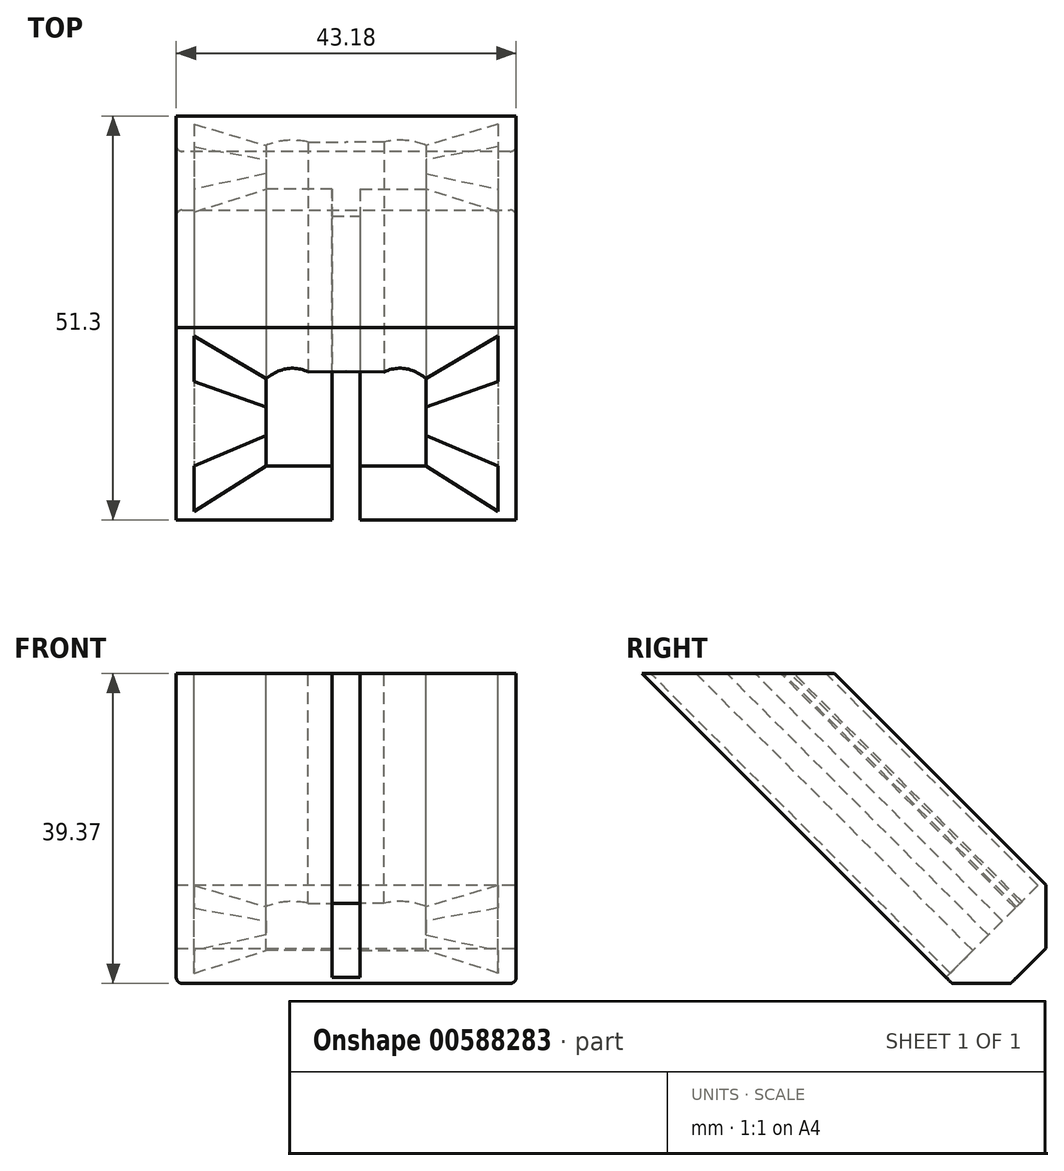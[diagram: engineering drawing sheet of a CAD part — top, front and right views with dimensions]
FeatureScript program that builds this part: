
annotation { "Feature Type Name" : "Feature", "Feature Type Description" : "" }
export const myFeature = defineFeature(function(context is Context, id is Id, definition is map)
    precondition{}
    {
        {
            var Q0;
            Q0=qCreatedBy(makeId("Front.planeOp"),FACE);
            var sketch = newSketch(context, id + "F0", { "sketchPlane" : qUnion([Q0])});
            skLineSegment(sketch, "E0.bottom", {"start": v(21.59, -8.64) * mm, "end": v(-21.6, -8.64) * mm});
            skLineSegment(sketch, "E0.top", {"start": v(21.59, 8.64) * mm, "end": v(-21.59, 8.64) * mm});
            skLineSegment(sketch, "E0.left", {"start": v(21.59, -8.64) * mm, "end": v(21.59, 8.64) * mm});
            skLineSegment(sketch, "E0.right", {"start": v(-21.6, -8.64) * mm, "end": v(-21.59, 8.64) * mm});
            skPoint(sketch, "E0.middle", {"position": v(0, 0) * mm});
            skSolve(sketch);
        }
        {
            var Q0;
            Q0=qCreatedBy(makeId("Front.planeOp"),FACE);
            var sketch = newSketch(context, id + "F1", { "sketchPlane" : qUnion([Q0])});
            skPoint(sketch, "E1.middle", {"position": v(0, 0) * mm});
            skLineSegment(sketch, "E2.left", {"start": v(10.16, 1.5) * mm, "end": v(10.16, -1.03) * mm});
            skLineSegment(sketch, "E3", {"start": v(19.3, 3.81) * mm, "end": v(10.16, 1.5) * mm});
            skLineSegment(sketch, "E4", {"start": v(10.16, -1.03) * mm, "end": v(19.3, -3.81) * mm});
            skLineSegment(sketch, "E5.left", {"start": v(19.3, 7.87) * mm, "end": v(19.3, 3.81) * mm});
            skLineSegment(sketch, "E6", {"start": v(19.3, -7.87) * mm, "end": v(10.16, -3.81) * mm});
            skLineSegment(sketch, "E7", {"start": v(19.3, 7.87) * mm, "end": v(10.16, 4.05) * mm});
            skLineSegment(sketch, "E8", {"start": v(1.78, -7.87) * mm, "end": v(1.78, -3.81) * mm});
            skLineSegment(sketch, "E9.trimOffspring", {"start": v(1.78, -3.81) * mm, "end": v(10.16, -3.81) * mm});
            skLineSegment(sketch, "E10.trimOffspring", {"start": v(19.3, -3.8) * mm, "end": v(19.3, -7.87) * mm});
            skLineSegment(sketch, "E11", {"start": v(1.78, -7.87) * mm, "end": v(1.78, -8.98) * mm});
            skArc(sketch, "E12", {"start": v(10.16, 4.05) * mm, "mid": v(7.57, 4.95) * mm, "end": v(4.83, 4.67) * mm});
            skLineSegment(sketch, "E13", {"start": v(4.83, 4.67) * mm, "end": v(0, 4.69) * mm});
            skLineSegment(sketch, "E14.MirrorCS", {"start": v(-10.16, 1.5) * mm, "end": v(-10.16, -1.03) * mm});
            skLineSegment(sketch, "E15.MirrorCS", {"start": v(-10.16, -1.03) * mm, "end": v(-19.3, -3.81) * mm});
            skLineSegment(sketch, "E16.MirrorCS", {"start": v(-19.3, -3.8) * mm, "end": v(-19.3, -7.87) * mm});
            skLineSegment(sketch, "E17.MirrorCS", {"start": v(-1.78, -7.87) * mm, "end": v(-1.78, -3.81) * mm});
            skLineSegment(sketch, "E18.MirrorCS", {"start": v(-4.83, 4.67) * mm, "end": v(0, 4.69) * mm});
            skLineSegment(sketch, "E19.MirrorCS", {"start": v(-1.78, -7.87) * mm, "end": v(-1.78, -8.98) * mm});
            skLineSegment(sketch, "E20.MirrorCS", {"start": v(-19.3, -7.87) * mm, "end": v(-10.16, -3.81) * mm});
            skLineSegment(sketch, "E21.MirrorCS", {"start": v(-19.3, 3.81) * mm, "end": v(-10.16, 1.5) * mm});
            skLineSegment(sketch, "E22.MirrorCS", {"start": v(-19.3, 7.87) * mm, "end": v(-10.16, 4.05) * mm});
            skArc(sketch, "E23.MirrorCS", {"start": v(-10.16, 4.05) * mm, "mid": v(-7.57, 4.95) * mm, "end": v(-4.83, 4.67) * mm});
            skLineSegment(sketch, "E24.MirrorCS", {"start": v(-19.3, 7.87) * mm, "end": v(-19.3, 3.81) * mm});
            skLineSegment(sketch, "E25.MirrorCS", {"start": v(-1.78, -3.81) * mm, "end": v(-10.16, -3.81) * mm});
            skLineSegment(sketch, "E26", {"start": v(-1.78, -8.98) * mm, "end": v(1.78, -8.98) * mm});
            skSolve(sketch);
        }
        {
            var Q0;
            Q0=makeQuery(id+"F0.imprint","IMPRINT",FACE,{"disambiguationData":[TD([[makeQuery(id+"F0.imprint","IMPRINT",EDGE,{"derivedFrom":sQuery(id+"F0.wireOp",EDGE,"E0.bottom")}),-1.0]])]});
            extrude(context, id + "F2", {"entities" : qUnion([Q0]), "oppositeDirection" : true, "depth" : 76.2 * mm, "offsetDistance" : 25.4 * mm});
        }
        {
            var Q0;
            Q0 = qSketchRegion(id + "F1", true);
            extrude(context, id + "F3", {"entities" : qUnion([Q0]), "operationType" : NewBodyOperationType.REMOVE, "oppositeDirection" : true, "depth" : 69.85 * mm, "offsetDistance" : 25.4 * mm});
        }
        {
            var Q0;
            Q0=makeQuery(id+"F2.opExtrude","SWEPT_BODY",BODY,{"disambiguationData":[OSD([sQuery(id+"F0.wireOp",EDGE,"E0.bottom"),sQuery(id+"F0.wireOp",EDGE,"E0.top"),sQuery(id+"F0.wireOp",EDGE,"E0.left"),sQuery(id+"F0.wireOp",EDGE,"E0.right")])]});
            var Q1;
            Q1=qCreatedBy(makeId("Front.planeOp"),FACE);
            transform(context, id + "F4", {"entities" : qUnion([Q0]), "transformType" : TransformType.TRANSLATION_DISTANCE, "transformDirection" : qUnion([Q1]), "distance" : 38.1 * mm, "makeCopy" : false});
        }
        {
            var Q0;
            Q0=qCreatedBy(makeId("Top.planeOp"),FACE);
            var sketch = newSketch(context, id + "F5", { "sketchPlane" : qUnion([Q0])});
            skLineSegment(sketch, "E27", {"start": v(0, 0) * mm, "end": v(38.76, 0) * mm});
            skLineSegment(sketch, "E28", {"start": v(38.76, 0) * mm, "end": v(-47.09, 0) * mm});
            skSolve(sketch);
        }
        {
            var Q0;
            Q0=makeQuery(id+"F2.opExtrude","SWEPT_BODY",BODY,{"disambiguationData":[OSD([sQuery(id+"F0.wireOp",EDGE,"E0.bottom"),sQuery(id+"F0.wireOp",EDGE,"E0.top"),sQuery(id+"F0.wireOp",EDGE,"E0.left"),sQuery(id+"F0.wireOp",EDGE,"E0.right")])]});
            var Q1;
            Q1=sQuery(id+"F5.wireOp",EDGE,"E28");
            transform(context, id + "F6", {"entities" : qUnion([Q0]), "transformType" : TransformType.ROTATION, "transformAxis" : qUnion([Q1]), "angle" : 45 * degree, "makeCopy" : false});
        }
        {
            var Q0;
            Q0=makeQuery(id+"F3.boolean.opBoolean","COPY",FACE,{"derivedFrom":makeQuery(id+"F3.opExtrude","SWEPT_FACE",FACE,{"disambiguationData":[OSD([sQuery(id+"F1.wireOp",EDGE,"E14.MirrorCS")])]})});
            var sketch = newSketch(context, id + "F7", { "sketchPlane" : qUnion([Q0])});
            skPoint(sketch, "E29", {"position": v(28.02, -16.88) * mm});
            skLineSegment(sketch, "E30", {"start": v(28.02, -16.88) * mm, "end": v(28.02, -16.88) * mm});
            skLineSegment(sketch, "E31", {"start": v(28.02, -16.88) * mm, "end": v(28.02, -40.69) * mm});
            skLineSegment(sketch, "E32", {"start": v(28.02, -16.88) * mm, "end": v(36.21, -8.69) * mm});
            skPoint(sketch, "E33", {"position": v(22.62, -22.28) * mm});
            skLineSegment(sketch, "E34", {"start": v(22.62, -22.28) * mm, "end": v(-9.7, 10.05) * mm});
            skLineSegment(sketch, "E35", {"start": v(-9.7, 10.05) * mm, "end": v(-25.67, -5.9) * mm});
            skLineSegment(sketch, "E36", {"start": v(-25.67, -5.9) * mm, "end": v(0, 19.76) * mm});
            skSolve(sketch);
        }
        {
            var Q0;
            Q0=qCreatedBy(makeId("Right.planeOp"),FACE);
            var sketch = newSketch(context, id + "F8", { "sketchPlane" : qUnion([Q0])});
            skPoint(sketch, "E37", {"position": v(-9.7, 10.05) * mm});
            skPoint(sketch, "E38", {"position": v(29.04, -17.4) * mm});
            skLineSegment(sketch, "E39", {"start": v(-39.87, 10.05) * mm, "end": v(29.04, 10.05) * mm});
            skLineSegment(sketch, "E40", {"start": v(29.04, -29.32) * mm, "end": v(-39.87, -29.32) * mm});
            skLineSegment(sketch, "E41", {"start": v(29.04, 10.05) * mm, "end": v(29.04, -29.32) * mm});
            skLineSegment(sketch, "E42", {"start": v(-39.87, 10.05) * mm, "end": v(-39.87, -29.32) * mm});
            skLineSegment(sketch, "E43.bottom", {"start": v(42.4, -44.6) * mm, "end": v(-54.78, -44.6) * mm});
            skLineSegment(sketch, "E43.top", {"start": v(42.4, 36.37) * mm, "end": v(-54.78, 36.37) * mm});
            skLineSegment(sketch, "E43.left", {"start": v(42.4, -44.6) * mm, "end": v(42.4, 36.37) * mm});
            skLineSegment(sketch, "E43.right", {"start": v(-54.78, -44.6) * mm, "end": v(-54.78, 36.37) * mm});
            skSolve(sketch);
        }
        {
            var Q0;
            Q0 = qSketchRegion(id + "F8", true);
            extrude(context, id + "F9", {"entities" : qUnion([Q0]), "operationType" : NewBodyOperationType.REMOVE, "endBound" : BoundingType.SYMMETRIC, "oppositeDirection" : true, "depth" : 76.2 * mm, "offsetDistance" : 25.4 * mm});
        }
        {
            var Q0;
            Q0=makeQuery(id+"F9.boolean.opBoolean","INTERSECT",EDGE,{"derivedFrom":[makeQuery(id+"F2.opExtrude","SWEPT_FACE",FACE,{"disambiguationData":[OSD([sQuery(id+"F0.wireOp",EDGE,"E0.left")])]}),makeQuery(id+"F9.opExtrude","SWEPT_FACE",FACE,{"disambiguationData":[OSD([sQuery(id+"F8.wireOp",EDGE,"E40")])]})]});
            var Q1;
            Q1=makeQuery(id+"F9.boolean.opBoolean","INTERSECT",EDGE,{"derivedFrom":[makeQuery(id+"F2.opExtrude","SWEPT_FACE",FACE,{"disambiguationData":[OSD([sQuery(id+"F0.wireOp",EDGE,"E0.right")])]}),makeQuery(id+"F9.opExtrude","SWEPT_FACE",FACE,{"disambiguationData":[OSD([sQuery(id+"F8.wireOp",EDGE,"E40")])]})]});
            fillet(context, id + "F10", {"entities" : qUnion([Q0, Q1]), "radius" : 0.76 * mm, "tangentPropagation" : true, "allowEdgeOverflow" : false});
        }
    });
